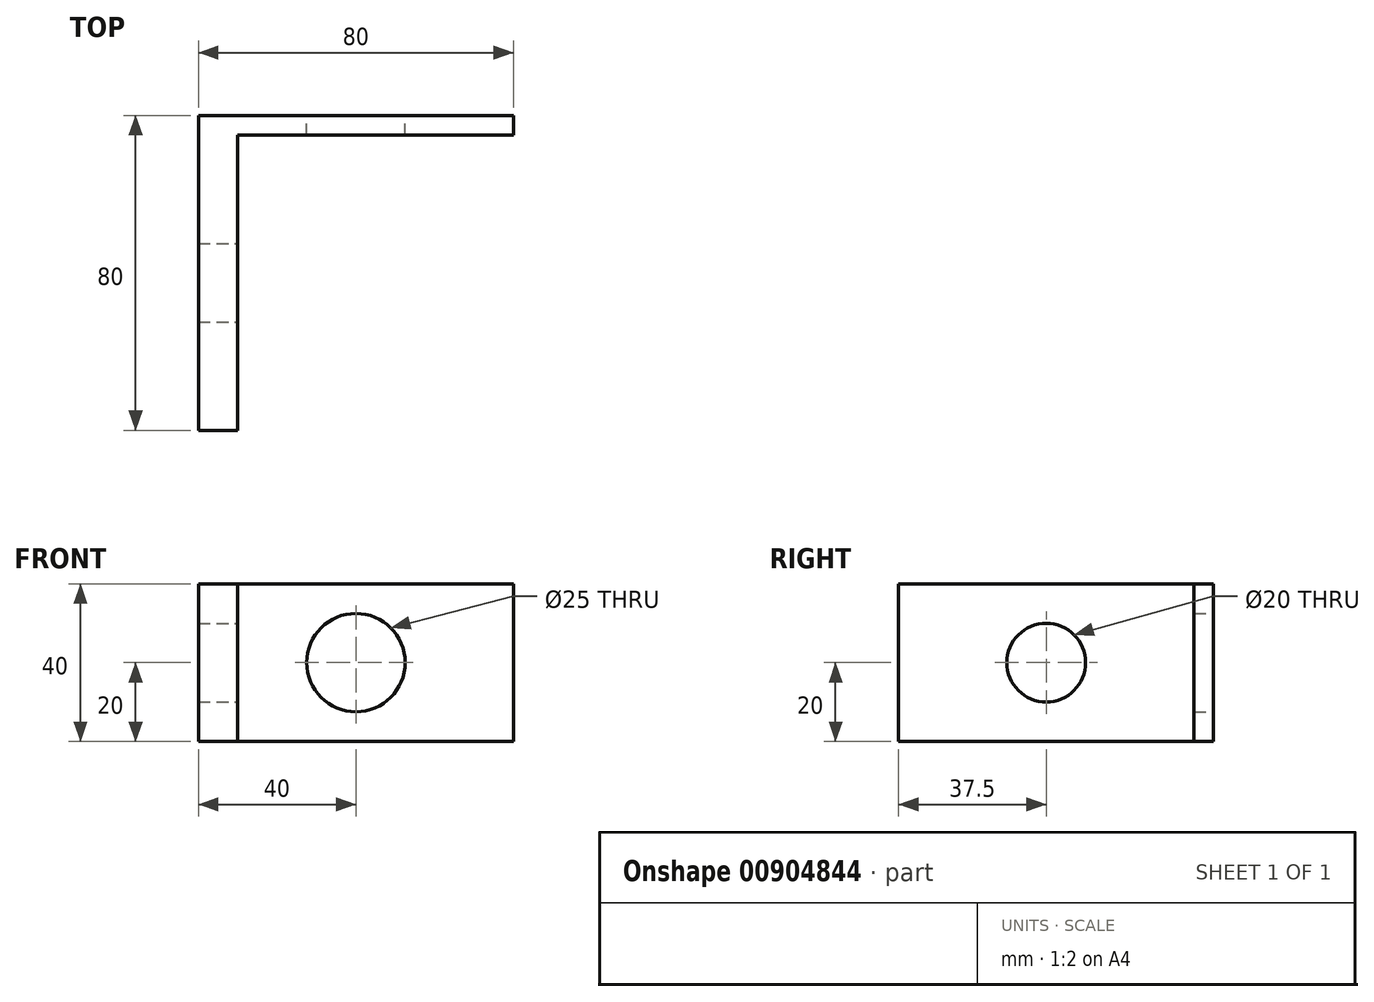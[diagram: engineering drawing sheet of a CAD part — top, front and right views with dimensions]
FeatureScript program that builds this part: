
annotation { "Feature Type Name" : "Feature", "Feature Type Description" : "" }
export const myFeature = defineFeature(function(context is Context, id is Id, definition is map)
    precondition{}
    {
        {
            var Q0;
            Q0=qCreatedBy(makeId("Front.planeOp"),FACE);
            var sketch = newSketch(context, id + "F0", { "sketchPlane" : qUnion([Q0])});
            skLineSegment(sketch, "E0.bottom", {"start": v(40, -20) * mm, "end": v(-40, -20) * mm});
            skLineSegment(sketch, "E0.top", {"start": v(40, 20) * mm, "end": v(-40, 20) * mm});
            skLineSegment(sketch, "E0.left", {"start": v(40, -20) * mm, "end": v(40, 20) * mm});
            skLineSegment(sketch, "E0.right", {"start": v(-40, -20) * mm, "end": v(-40, 20) * mm});
            skPoint(sketch, "E0.middle", {"position": v(0, 0) * mm});
            skCircle(sketch, "E1", {"center": v(0, 0) * mm, "radius": 12.5 * mm});
            skSolve(sketch);
        }
        {
            var Q0;
            Q0=makeQuery(id+"F0.imprint","IMPRINT",FACE,{"disambiguationData":[TD([[makeQuery(id+"F0.imprint","IMPRINT",EDGE,{"derivedFrom":sQuery(id+"F0.wireOp",EDGE,"E0.bottom")}),-1.0]])]});
            extrude(context, id + "F1", {"entities" : qUnion([Q0]), "depth" : 5 * mm, "offsetDistance" : 25 * mm});
        }
        {
            var Q0;
            Q0=makeQuery(id+"F1.opExtrude","CAP_FACE",FACE,{"disambiguationData":[OSD([sQuery(id+"F0.wireOp",EDGE,"E0.bottom"),sQuery(id+"F0.wireOp",EDGE,"E0.top"),sQuery(id+"F0.wireOp",EDGE,"E0.left"),sQuery(id+"F0.wireOp",EDGE,"E0.right"),sQuery(id+"F0.wireOp",EDGE,"E1")])],"isStart":false});
            var sketch = newSketch(context, id + "F2", { "sketchPlane" : qUnion([Q0])});
            skLineSegment(sketch, "E2.bottom", {"start": v(-40, 20) * mm, "end": v(-30, 20) * mm});
            skLineSegment(sketch, "E2.top", {"start": v(-40, -20) * mm, "end": v(-30, -20) * mm});
            skLineSegment(sketch, "E2.left", {"start": v(-40, 20) * mm, "end": v(-40, -20) * mm});
            skLineSegment(sketch, "E2.right", {"start": v(-30, 20) * mm, "end": v(-30, -20) * mm});
            skSolve(sketch);
        }
        {
            var Q0;
            Q0=makeQuery(id+"F2.imprint","IMPRINT",FACE,{"disambiguationData":[TD([[makeQuery(id+"F2.imprint","IMPRINT",EDGE,{"derivedFrom":sQuery(id+"F2.wireOp",EDGE,"E2.bottom")}),1.0]])]});
            extrude(context, id + "F3", {"entities" : qUnion([Q0]), "operationType" : NewBodyOperationType.ADD, "depth" : 75 * mm, "offsetDistance" : 25 * mm});
        }
        {
            var Q0;
            Q0=makeQuery(id+"F3.opExtrude","SWEPT_FACE",FACE,{"disambiguationData":[OSD([sQuery(id+"F2.wireOp",EDGE,"E2.right")])]});
            var sketch = newSketch(context, id + "F4", { "sketchPlane" : qUnion([Q0])});
            skPoint(sketch, "E3", {"position": v(-42.5, -20) * mm});
            skPoint(sketch, "E4", {"position": v(-42.5, 20) * mm});
            skPoint(sketch, "E5", {"position": v(-80, 0) * mm});
            skLineSegment(sketch, "E6", {"start": v(-42.5, 20) * mm, "end": v(-42.5, -20) * mm});
            skPoint(sketch, "E7", {"position": v(-42.5, 0) * mm});
            skCircle(sketch, "E8", {"center": v(-42.5, 0) * mm, "radius": 10 * mm});
            skSolve(sketch);
        }
        {
            var Q0;
            {var subQ0=sQuery(id+"F4.wireOp",EDGE,"E8");var subQ1=sQuery(id+"F4.wireOp",EDGE,"E6");var subQ2=makeQuery(id+"F4.imprint","INTERSECT",VERTEX,{"disambiguationData":[OD(0.0)],"derivedFrom":[subQ1,subQ0]});Q0=makeQuery(id+"F4.imprint","IMPRINT",FACE,{"disambiguationData":[TD([[makeQuery(id+"F4.imprint","IMPRINT",EDGE,{"disambiguationData":[TD([[subQ2,-1.0]])],"derivedFrom":subQ1}),1.0]])]});}
            var Q1;
            {var subQ0=sQuery(id+"F4.wireOp",EDGE,"E8");var subQ1=sQuery(id+"F4.wireOp",EDGE,"E6");var subQ2=makeQuery(id+"F4.imprint","INTERSECT",VERTEX,{"disambiguationData":[OD(0.0)],"derivedFrom":[subQ1,subQ0]});Q1=makeQuery(id+"F4.imprint","IMPRINT",FACE,{"disambiguationData":[TD([[makeQuery(id+"F4.imprint","IMPRINT",EDGE,{"disambiguationData":[TD([[subQ2,-1.0]])],"derivedFrom":subQ1}),-1.0]])]});}
            extrude(context, id + "F5", {"entities" : qUnion([Q0, Q1]), "operationType" : NewBodyOperationType.REMOVE, "endBound" : BoundingType.THROUGH_ALL, "oppositeDirection" : true, "depth" : 25 * mm, "offsetDistance" : 25 * mm});
        }
    });
